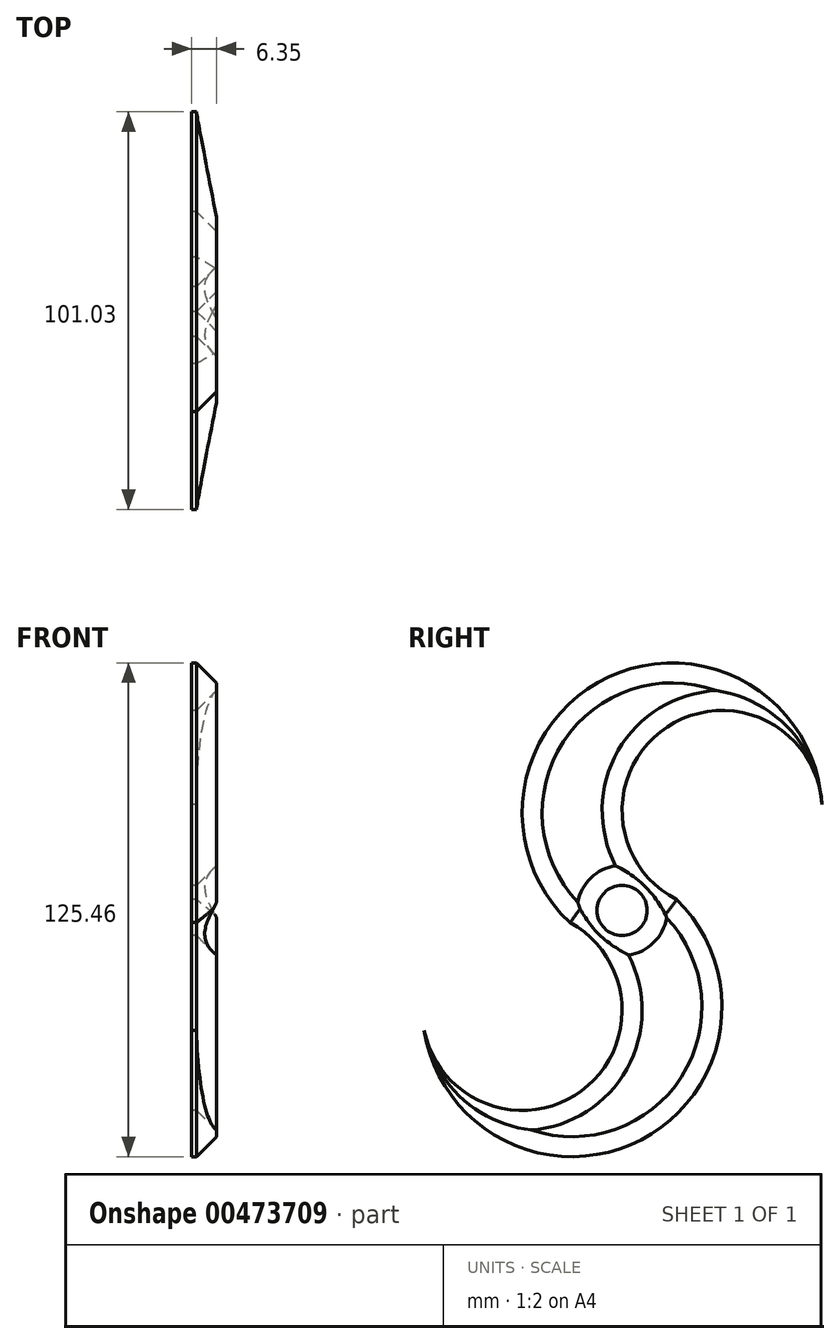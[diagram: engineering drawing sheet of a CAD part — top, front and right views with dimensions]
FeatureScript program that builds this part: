
annotation { "Feature Type Name" : "Feature", "Feature Type Description" : "" }
export const myFeature = defineFeature(function(context is Context, id is Id, definition is map)
    precondition{}
    {
        {
            var Q0;
            Q0=qCreatedBy(makeId("Right.planeOp"),FACE);
            var sketch = newSketch(context, id + "F0", { "sketchPlane" : qUnion([Q0])});
            skCircle(sketch, "E0", {"center": v(25.4, 25.4) * mm, "radius": 25.4 * mm});
            skCircle(sketch, "E1", {"center": v(-25.4, -25.4) * mm, "radius": 25.4 * mm});
            skArc(sketch, "E2", {"start": v(50.75, 26.93) * mm, "mid": v(-6.83, 57.5) * mm, "end": v(-7.2, -7.7) * mm});
            skArc(sketch, "E3", {"start": v(-50.28, -30.53) * mm, "mid": v(8.76, -55.94) * mm, "end": v(6.62, 8.3) * mm});
            skPoint(sketch, "E4.middle", {"position": v(0, 0) * mm});
            skLineSegment(sketch, "E5.bottom", {"start": v(4.55, -4.44) * mm, "end": v(-4.34, -4.45) * mm});
            skLineSegment(sketch, "E5.top", {"start": v(4.55, 4.45) * mm, "end": v(-4.34, 4.44) * mm});
            skLineSegment(sketch, "E5.left", {"start": v(4.55, -4.44) * mm, "end": v(4.55, 4.45) * mm});
            skLineSegment(sketch, "E5.right", {"start": v(-4.34, -4.44) * mm, "end": v(-4.34, 4.44) * mm});
            skCircle(sketch, "E6", {"center": v(0, 0) * mm, "radius": 6.36 * mm});
            skSolve(sketch);
        }
        {
            var Q0;
            {var subQ0=sQuery(id+"F0.wireOp",EDGE,"E2");var subQ5=sQuery(id+"F0.wireOp",EDGE,"E0");var subQ9=makeQuery(id+"F0.imprint","INTERSECT",VERTEX,{"derivedFrom":[subQ5,subQ0]});Q0=makeQuery(id+"F0.imprint","IMPRINT",FACE,{"disambiguationData":[TD([[makeQuery(id+"F0.imprint","IMPRINT",EDGE,{"disambiguationData":[TD([[subQ9,-1.0]])],"derivedFrom":subQ5}),-1.0]])]});}
            extrude(context, id + "F1", {"entities" : qUnion([Q0]), "offsetDistance" : 25.4 * mm, "depth" : 6.35 * mm});
        }
        {
            var Q0;
            Q0=makeQuery(id+"F1.opExtrude","CAP_FACE",FACE,{"disambiguationData":[OSD([sQuery(id+"F0.wireOp",EDGE,"E0"),sQuery(id+"F0.wireOp",EDGE,"E1"),sQuery(id+"F0.wireOp",EDGE,"E2"),sQuery(id+"F0.wireOp",EDGE,"E3"),sQuery(id+"F0.wireOp",EDGE,"Xat1jKPF-Fe9H-bH5e-zruu-CCDd8t2GPS8e")])],"isStart":false});
            chamfer(context, id + "F2", {"entities" : qUnion([Q0]), "width" : 5.08 * mm, "tangentPropagation" : true});
        }
    });
